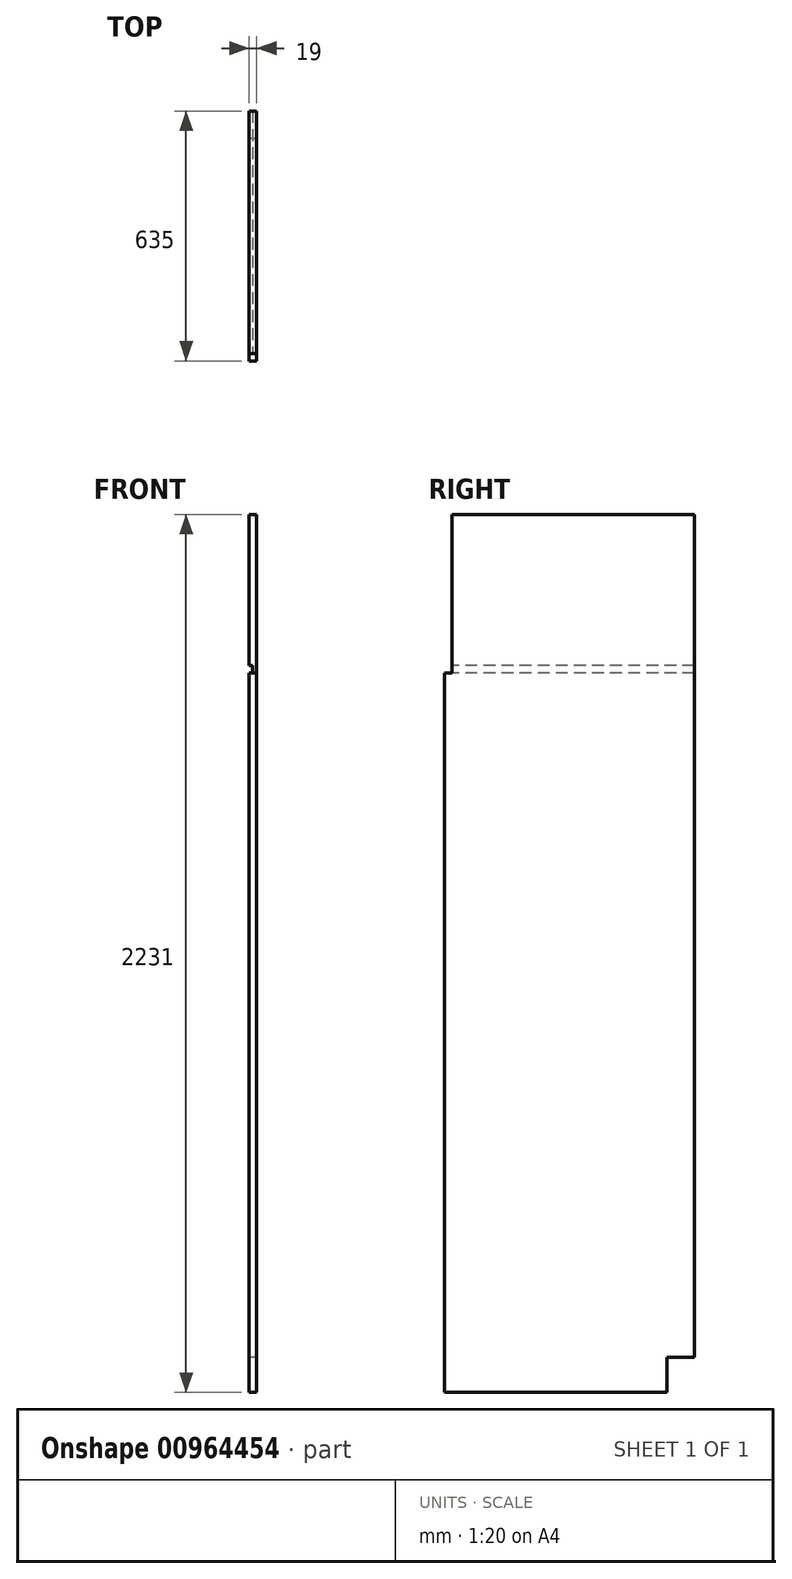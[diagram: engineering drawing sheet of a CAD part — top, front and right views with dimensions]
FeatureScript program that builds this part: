
annotation { "Feature Type Name" : "Feature", "Feature Type Description" : "" }
export const myFeature = defineFeature(function(context is Context, id is Id, definition is map)
    precondition{}
    {
        {
            var Q0;
            Q0=qCreatedBy(makeId("Right.planeOp"),FACE);
            var sketch = newSketch(context, id + "F0", { "sketchPlane" : qUnion([Q0])});
            skLineSegment(sketch, "E0.bottom", {"start": v(0, 0) * mm, "end": v(635, 0) * mm});
            skLineSegment(sketch, "E0.top", {"start": v(0, 2231) * mm, "end": v(635, 2231) * mm});
            skLineSegment(sketch, "E0.left", {"start": v(0, 0) * mm, "end": v(0, 2231) * mm});
            skLineSegment(sketch, "E0.right", {"start": v(635, 0) * mm, "end": v(635, 2231) * mm});
            skSolve(sketch);
        }
        {
            var Q0;
            Q0=makeQuery(id+"F0.imprint","IMPRINT",FACE,{"disambiguationData":[TD([[makeQuery(id+"F0.imprint","IMPRINT",EDGE,{"derivedFrom":sQuery(id+"F0.wireOp",EDGE,"E0.bottom")}),1.0]])]});
            extrude(context, id + "F1", {"entities" : qUnion([Q0]), "depth" : 19 * mm, "offsetDistance" : 25 * mm});
        }
        {
            var Q0;
            Q0=qCreatedBy(makeId("Front.planeOp"),FACE);
            var sketch = newSketch(context, id + "F2", { "sketchPlane" : qUnion([Q0])});
            skLineSegment(sketch, "E1.bottom", {"start": v(0, 1828) * mm, "end": v(9, 1828) * mm});
            skLineSegment(sketch, "E1.top", {"start": v(0, 1847) * mm, "end": v(9, 1847) * mm});
            skLineSegment(sketch, "E1.left", {"start": v(0, 1828) * mm, "end": v(0, 1847) * mm});
            skLineSegment(sketch, "E1.right", {"start": v(9, 1828) * mm, "end": v(9, 1847) * mm});
            skSolve(sketch);
        }
        {
            var Q0;
            Q0 = qSketchRegion(id + "F2", true);
            extrude(context, id + "F3", {"entities" : qUnion([Q0]), "operationType" : NewBodyOperationType.REMOVE, "endBound" : BoundingType.THROUGH_ALL, "oppositeDirection" : true, "depth" : 25 * mm, "offsetDistance" : 25 * mm});
        }
        {
            var Q0;
            Q0=qCreatedBy(makeId("Right.planeOp"),FACE);
            var sketch = newSketch(context, id + "F4", { "sketchPlane" : qUnion([Q0])});
            skLineSegment(sketch, "E2.bottom", {"start": v(0, 0) * mm, "end": v(75, 0) * mm, "construction": true});
            skLineSegment(sketch, "E2.top", {"start": v(0, 90) * mm, "end": v(75, 90) * mm, "construction": true});
            skLineSegment(sketch, "E2.left", {"start": v(0, 0) * mm, "end": v(0, 90) * mm, "construction": true});
            skLineSegment(sketch, "E2.right", {"start": v(75, 0) * mm, "end": v(75, 90) * mm, "construction": true});
            skLineSegment(sketch, "E3.bottom", {"start": v(635, 0) * mm, "end": v(565, 0) * mm});
            skLineSegment(sketch, "E3.top", {"start": v(635, 90) * mm, "end": v(565, 90) * mm});
            skLineSegment(sketch, "E3.left", {"start": v(635, 0) * mm, "end": v(635, 90) * mm});
            skLineSegment(sketch, "E3.right", {"start": v(565, 0) * mm, "end": v(565, 90) * mm});
            skSolve(sketch);
        }
        {
            var Q0;
            Q0 = qSketchRegion(id + "F4", true);
            extrude(context, id + "F5", {"entities" : qUnion([Q0]), "operationType" : NewBodyOperationType.REMOVE, "endBound" : BoundingType.THROUGH_ALL, "depth" : 25 * mm, "offsetDistance" : 25 * mm});
        }
        {
            var Q0;
            Q0=qCreatedBy(makeId("Right.planeOp"),FACE);
            var sketch = newSketch(context, id + "F6", { "sketchPlane" : qUnion([Q0])});
            skLineSegment(sketch, "E4.bottom", {"start": v(0, 1828) * mm, "end": v(19, 1828) * mm});
            skLineSegment(sketch, "E4.top", {"start": v(0, 2231) * mm, "end": v(19, 2231) * mm});
            skLineSegment(sketch, "E4.left", {"start": v(0, 1828) * mm, "end": v(0, 2231) * mm});
            skLineSegment(sketch, "E4.right", {"start": v(19, 1828) * mm, "end": v(19, 2231) * mm});
            skSolve(sketch);
        }
        {
            var Q0;
            Q0 = qSketchRegion(id + "F6", true);
            extrude(context, id + "F7", {"entities" : qUnion([Q0]), "operationType" : NewBodyOperationType.REMOVE, "endBound" : BoundingType.THROUGH_ALL, "depth" : 25 * mm, "offsetDistance" : 25 * mm});
        }
    });
